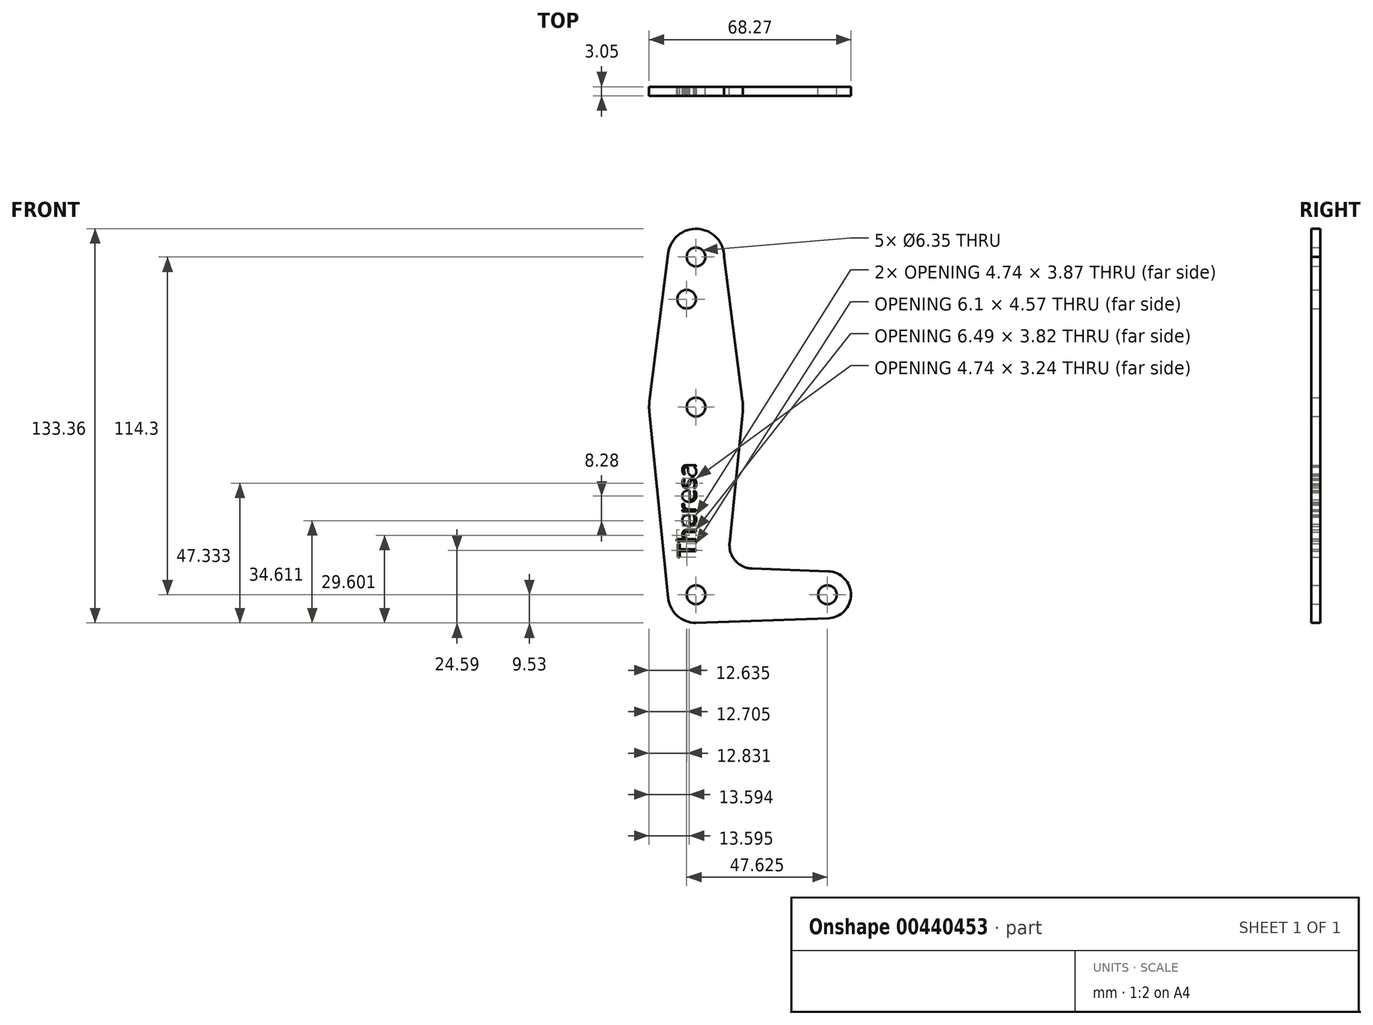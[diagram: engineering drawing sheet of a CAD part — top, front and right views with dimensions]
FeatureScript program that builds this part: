
annotation { "Feature Type Name" : "Feature", "Feature Type Description" : "" }
export const myFeature = defineFeature(function(context is Context, id is Id, definition is map)
    precondition{}
    {
        {
            var Q0;
            Q0=qCreatedBy(makeId("Front.planeOp"),FACE);
            var sketch = newSketch(context, id + "F0", { "sketchPlane" : qUnion([Q0])});
            skLineSegment(sketch, "E0", {"start": v(0, 114.3) * mm, "end": v(0, 0) * mm, "construction": true});
            skLineSegment(sketch, "E1", {"start": v(0, 0) * mm, "end": v(44.45, 0) * mm, "construction": true});
            skCircle(sketch, "E2", {"center": v(0, 114.3) * mm, "radius": 9.53 * mm});
            skCircle(sketch, "E3", {"center": v(0, 63.5) * mm, "radius": 15.88 * mm});
            skCircle(sketch, "E4", {"center": v(0, 0) * mm, "radius": 9.53 * mm});
            skCircle(sketch, "E5", {"center": v(44.45, 0) * mm, "radius": 7.94 * mm});
            skLineSegment(sketch, "E6", {"start": v(-15.75, 65.48) * mm, "end": v(-9.45, 115.5) * mm});
            skLineSegment(sketch, "E7", {"start": v(0, -9.53) * mm, "end": v(44.73, -7.93) * mm});
            skLineSegment(sketch, "E8", {"start": v(18.97, 8.85) * mm, "end": v(44.73, 7.93) * mm});
            skLineSegment(sketch, "E9", {"start": v(9.52, 114.3) * mm, "end": v(15.75, 65.5) * mm});
            skLineSegment(sketch, "E10", {"start": v(15.8, 61.91) * mm, "end": v(11.34, 17.6) * mm});
            skCircle(sketch, "E11", {"center": v(-3.18, 100.03) * mm, "radius": 3.18 * mm});
            skCircle(sketch, "E12", {"center": v(0, 114.3) * mm, "radius": 3.18 * mm});
            skCircle(sketch, "E13", {"center": v(0, 63.5) * mm, "radius": 3.18 * mm});
            skCircle(sketch, "E14", {"center": v(0, 0) * mm, "radius": 3.18 * mm});
            skCircle(sketch, "E15", {"center": v(44.45, 0) * mm, "radius": 3.18 * mm});
            skArc(sketch, "E16.filletArc", {"start": v(11.34, 17.6) * mm, "mid": v(13.26, 11.57) * mm, "end": v(18.97, 8.85) * mm});
            skLineSegment(sketch, "E17", {"start": v(-15.8, 61.91) * mm, "end": v(-9.48, -0.95) * mm});
            skText(sketch, "E18", { "text": "Theresa", "fontName": "OpenSans-Regular.ttf"});
            const initialGuessF0  = {"E18": [0, 0.0127, 0, 1, 0.00615]};
            skSetInitialGuess(sketch, initialGuessF0);
            skSolve(sketch);
        }
        {
            var Q0;
            {var subQ1=sQuery(id+"F0.wireOp",EDGE,"E6");Q0=makeQuery(id+"F0.imprint","IMPRINT",FACE,{"disambiguationData":[TD([[makeQuery(id+"F0.imprint","IMPRINT",EDGE,{"derivedFrom":subQ1}),-1.0]])]});}
            var Q1;
            Q1=makeQuery(id+"F0.imprint","IMPRINT",FACE,{"disambiguationData":[TD([[makeQuery(id+"F0.imprint","IMPRINT",EDGE,{"derivedFrom":sQuery(id+"F0.wireOp",EDGE,"E13")}),-1.0]])]});
            var Q2;
            {var subQ6=sQuery(id+"F0.wireOp",EDGE,"E8");Q2=makeQuery(id+"F0.imprint","IMPRINT",FACE,{"disambiguationData":[TD([[makeQuery(id+"F0.imprint","IMPRINT",EDGE,{"derivedFrom":subQ6}),-1.0]])]});}
            var Q3;
            Q3=makeQuery(id+"F0.imprint","IMPRINT",FACE,{"disambiguationData":[TD([[makeQuery(id+"F0.imprint","IMPRINT",EDGE,{"derivedFrom":sQuery(id+"F0.wireOp",EDGE,"E14")}),-1.0]])]});
            var Q4;
            Q4=makeQuery(id+"F0.imprint","IMPRINT",FACE,{"disambiguationData":[TD([[makeQuery(id+"F0.imprint","IMPRINT",EDGE,{"derivedFrom":sQuery(id+"F0.wireOp",EDGE,"E15")}),-1.0]])]});
            var Q5;
            Q5=makeQuery(id+"F0.imprint","IMPRINT",FACE,{"disambiguationData":[TD([[makeQuery(id+"F0.imprint","IMPRINT",EDGE,{"derivedFrom":sQuery(id+"F0.wireOp",EDGE,"E12")}),-1.0]])]});
            extrude(context, id + "F1", {"entities" : qUnion([Q0, Q1, Q2, Q3, Q4, Q5]), "depth" : 3.05 * mm});
        }
    });
